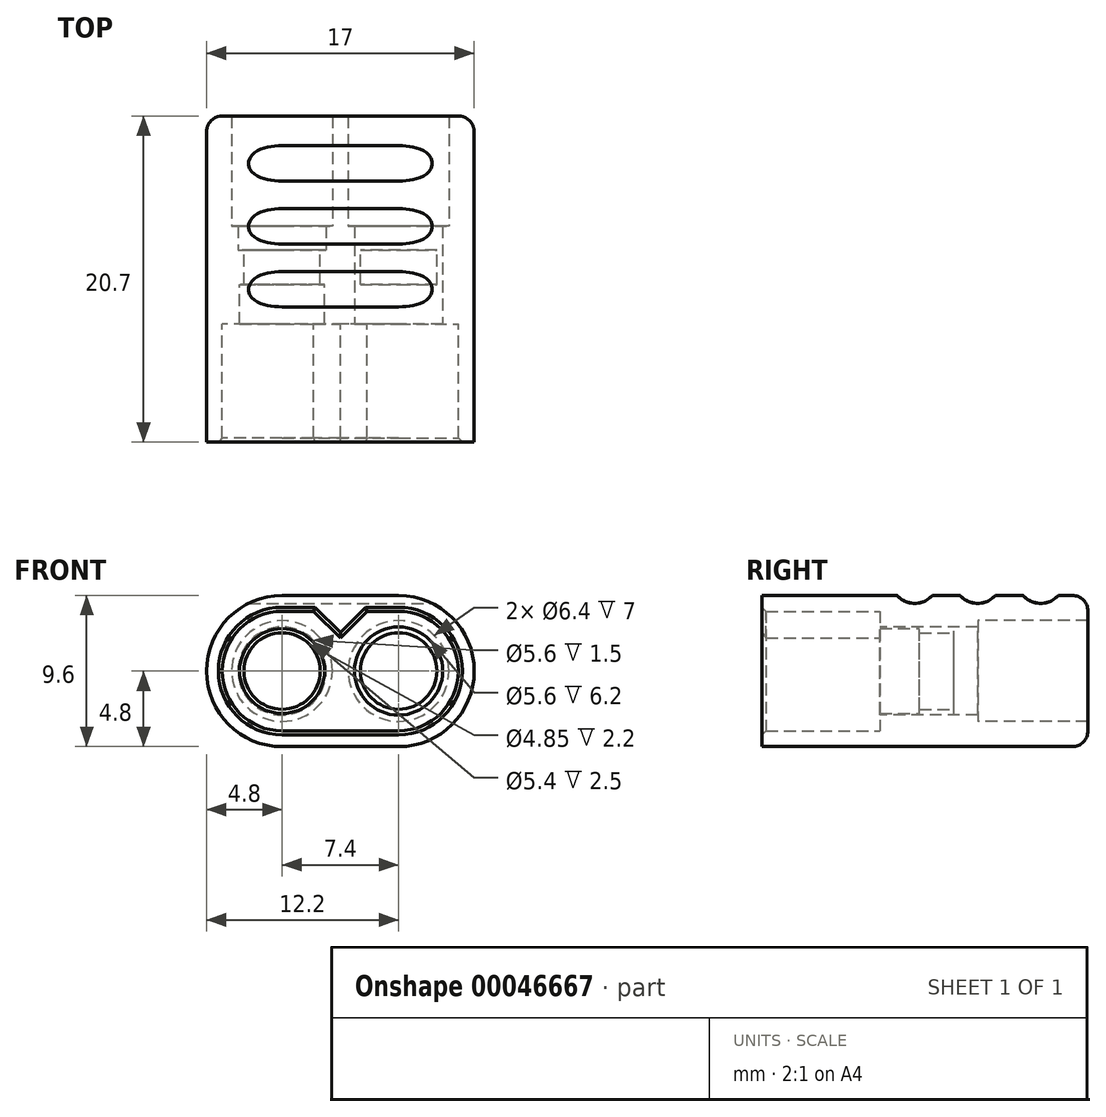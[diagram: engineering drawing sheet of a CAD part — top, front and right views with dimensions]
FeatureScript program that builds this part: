
annotation { "Feature Type Name" : "Feature", "Feature Type Description" : "" }
export const myFeature = defineFeature(function(context is Context, id is Id, definition is map)
    precondition{}
    {
        {
            var Q0;
            Q0=qCreatedBy(makeId("Front.planeOp"),FACE);
            var sketch = newSketch(context, id + "F0", { "sketchPlane" : qUnion([Q0])});
            skCircle(sketch, "E0", {"center": v(-3.7, 0) * mm, "radius": 2.43 * mm});
            skCircle(sketch, "E1.MirrorC", {"center": v(-3.7, 0) * mm, "radius": 2.8 * mm});
            skLineSegment(sketch, "E2", {"start": v(0, 0) * mm, "end": v(-8.5, 0) * mm, "construction": true});
            skArc(sketch, "E3", {"start": v(-3.7, 4.8) * mm, "mid": v(-7.1, 3.4) * mm, "end": v(-8.5, 0) * mm});
            skLineSegment(sketch, "E4", {"start": v(0, 4.8) * mm, "end": v(0, 0) * mm, "construction": true});
            skLineSegment(sketch, "E5", {"start": v(-3.7, 4.8) * mm, "end": v(-3.7, 0) * mm, "construction": true});
            skCircle(sketch, "E6.MirrorC", {"center": v(3.7, 0) * mm, "radius": 2.43 * mm});
            skCircle(sketch, "E7.MirrorC", {"center": v(3.7, 0) * mm, "radius": 2.8 * mm});
            skLineSegment(sketch, "E8", {"start": v(-3.7, 4.8) * mm, "end": v(0, 4.8) * mm});
            skArc(sketch, "E9.MirrorCS", {"start": v(-3.7, -4.8) * mm, "mid": v(-7.1, -3.4) * mm, "end": v(-8.5, 0) * mm});
            skLineSegment(sketch, "E10.MirrorCS", {"start": v(-3.7, -4.8) * mm, "end": v(0, -4.8) * mm});
            skLineSegment(sketch, "E11.MirrorCS", {"start": v(3.7, 4.8) * mm, "end": v(0, 4.8) * mm});
            skArc(sketch, "E12.MirrorCS", {"start": v(3.7, 4.8) * mm, "mid": v(7.1, 3.4) * mm, "end": v(8.5, 0) * mm});
            skArc(sketch, "E13.MirrorCS", {"start": v(3.7, -4.8) * mm, "mid": v(7.1, -3.4) * mm, "end": v(8.5, 0) * mm});
            skLineSegment(sketch, "E14.MirrorCS", {"start": v(3.7, -4.8) * mm, "end": v(0, -4.8) * mm});
            skSolve(sketch);
        }
        {
            var Q0;
            Q0=makeQuery(id+"F0.imprint","IMPRINT",FACE,{"disambiguationData":[TD([[makeQuery(id+"F0.imprint","IMPRINT",EDGE,{"derivedFrom":sQuery(id+"F0.wireOp",EDGE,"E1.MirrorC")}),-1.0]])]});
            extrude(context, id + "F1", {"entities" : qUnion([Q0]), "oppositeDirection" : true, "depth" : 1.5 * mm});
        }
        {
            var Q0;
            Q0=makeQuery(id+"F0.imprint","IMPRINT",FACE,{"disambiguationData":[TD([[makeQuery(id+"F0.imprint","IMPRINT",EDGE,{"derivedFrom":sQuery(id+"F0.wireOp",EDGE,"E1.MirrorC")}),-1.0]])]});
            var Q1;
            Q1=makeQuery(id+"F0.imprint","IMPRINT",FACE,{"disambiguationData":[TD([[makeQuery(id+"F0.imprint","IMPRINT",EDGE,{"derivedFrom":sQuery(id+"F0.wireOp",EDGE,"E0")}),-1.0]])]});
            var Q2;
            Q2=makeQuery(id+"F0.imprint","IMPRINT",FACE,{"disambiguationData":[TD([[makeQuery(id+"F0.imprint","IMPRINT",EDGE,{"derivedFrom":sQuery(id+"F0.wireOp",EDGE,"E6.MirrorC")}),1.0]])]});
            extrude(context, id + "F2", {"entities" : qUnion([Q0, Q1, Q2]), "operationType" : NewBodyOperationType.ADD, "depth" : 2.2 * mm});
        }
        {
            var Q0;
            Q0=makeQuery(id+"F2.opExtrude","CAP_FACE",FACE,{"disambiguationData":[OSD([sQuery(id+"F0.wireOp",EDGE,"9af29b95-2ce9-48ef-83fd-eb93086e848a.bottom"),sQuery(id+"F0.wireOp",EDGE,"9af29b95-2ce9-48ef-83fd-eb93086e848a.top"),sQuery(id+"F0.wireOp",EDGE,"9af29b95-2ce9-48ef-83fd-eb93086e848a.left"),sQuery(id+"F0.wireOp",EDGE,"9af29b95-2ce9-48ef-83fd-eb93086e848a.right"),sQuery(id+"F0.wireOp",EDGE,"E0"),sQuery(id+"F0.wireOp",EDGE,"3bfeefd6-8ccf-4d28-93f8-2f2611132b7e0.MirrorC")])],"isStart":false});
            var sketch = newSketch(context, id + "F3", { "sketchPlane" : qUnion([Q0])});
            skCircle(sketch, "E15", {"center": v(-3.7, 0) * mm, "radius": 2.7 * mm});
            skCircle(sketch, "E16.MirrorC", {"center": v(3.7, 0) * mm, "radius": 2.7 * mm});
            skSolve(sketch);
        }
        {
            var Q0;
            Q0=makeQuery(id+"F3.imprint","IMPRINT",FACE,{"disambiguationData":[TD([[makeQuery(id+"F3.imprint","IMPRINT",EDGE,{"derivedFrom":sQuery(id+"F3.wireOp",EDGE,"E15")}),-1.0]])]});
            extrude(context, id + "F4", {"entities" : qUnion([Q0]), "operationType" : NewBodyOperationType.ADD, "depth" : 2.5 * mm});
        }
        {
            var Q0;
            Q0=makeQuery(id+"F4.opExtrude","CAP_FACE",FACE,{"disambiguationData":[OSD([sQuery(id+"F0.wireOp",EDGE,"6d7ef5f6-68e2-491c-bdb9-d34946de3217"),sQuery(id+"F0.wireOp",EDGE,"4a62e17a-e464-4ae6-85fd-e67879230d62"),sQuery(id+"F0.wireOp",EDGE,"d8da9cf0-fa24-4876-8edd-ab64fd6ac28d"),sQuery(id+"F0.wireOp",EDGE,"6ed2982d-5885-44c9-aeb3-c63c06cbabe1.filletArc"),sQuery(id+"F0.wireOp",EDGE,"ac0d3ca8-c71e-4b4c-905e-2867e2134c0f.filletArc"),sQuery(id+"F0.wireOp",EDGE,"db059e13-4987-40d7-b22c-4aa99c86301e0.MirrorCS"),sQuery(id+"F0.wireOp",EDGE,"21968229-6fcb-4818-9fba-464d6f3a7a490.MirrorCS"),sQuery(id+"F0.wireOp",EDGE,"27c3a9c7-bba5-4ce6-a0b2-ee3fde2fc81d0.MirrorCS"),sQuery(id+"F0.wireOp",EDGE,"74e78b0a-03c2-4682-ad69-f2b08288fff30.MirrorCS"),sQuery(id+"F0.wireOp",EDGE,"d6014dcf-48b1-47f5-9b02-8fcda7855cd30.MirrorCS"),sQuery(id+"F3.wireOp",EDGE,"E15"),sQuery(id+"F3.wireOp",EDGE,"3893830b-eff6-4bac-9637-d990255e7b810.MirrorC")])],"isStart":false});
            var sketch = newSketch(context, id + "F5", { "sketchPlane" : qUnion([Q0])});
            skLineSegment(sketch, "E17", {"start": v(-3.7, -3.8) * mm, "end": v(0, -3.8) * mm});
            skLineSegment(sketch, "E18", {"start": v(-1.7, 3.8) * mm, "end": v(0, 2.1) * mm});
            skArc(sketch, "E19", {"start": v(-3.7, 3.8) * mm, "mid": v(-7.5, 0) * mm, "end": v(-3.7, -3.8) * mm});
            skLineSegment(sketch, "E20", {"start": v(-3.7, 3.8) * mm, "end": v(-1.7, 3.8) * mm});
            skLineSegment(sketch, "E21.MirrorCS", {"start": v(1.7, 3.8) * mm, "end": v(0, 2.1) * mm});
            skLineSegment(sketch, "E22.MirrorCS", {"start": v(3.7, 3.8) * mm, "end": v(1.7, 3.8) * mm});
            skArc(sketch, "E23.MirrorCS", {"start": v(3.7, 3.8) * mm, "mid": v(7.5, 0) * mm, "end": v(3.7, -3.8) * mm});
            skLineSegment(sketch, "E24.MirrorCS", {"start": v(3.7, -3.8) * mm, "end": v(0, -3.8) * mm});
            skSolve(sketch);
        }
        {
            var Q0;
            Q0=makeQuery(id+"F5.imprint","IMPRINT",FACE,{"disambiguationData":[TD([[makeQuery(id+"F5.imprint","IMPRINT",EDGE,{"derivedFrom":sQuery(id+"F5.wireOp",EDGE,"E17")}),-1.0]])]});
            extrude(context, id + "F6", {"entities" : qUnion([Q0]), "operationType" : NewBodyOperationType.ADD, "depth" : 7.5 * mm});
        }
        {
            var Q0;
            Q0=makeQuery(id+"F1.opExtrude","CAP_FACE",FACE,{"disambiguationData":[OSD([sQuery(id+"F0.wireOp",EDGE,"E1.MirrorC"),sQuery(id+"F0.wireOp",EDGE,"E3"),sQuery(id+"F0.wireOp",EDGE,"E7.MirrorC"),sQuery(id+"F0.wireOp",EDGE,"E8"),sQuery(id+"F0.wireOp",EDGE,"E9.MirrorCS"),sQuery(id+"F0.wireOp",EDGE,"E10.MirrorCS"),sQuery(id+"F0.wireOp",EDGE,"E11.MirrorCS"),sQuery(id+"F0.wireOp",EDGE,"E12.MirrorCS"),sQuery(id+"F0.wireOp",EDGE,"E13.MirrorCS"),sQuery(id+"F0.wireOp",EDGE,"E14.MirrorCS")])],"isStart":false});
            var sketch = newSketch(context, id + "F7", { "sketchPlane" : qUnion([Q0])});
            skCircle(sketch, "E25", {"center": v(3.7, 0) * mm, "radius": 3.2 * mm});
            skCircle(sketch, "E26.MirrorC", {"center": v(-3.7, 0) * mm, "radius": 3.2 * mm});
            skSolve(sketch);
        }
        {
            var Q0;
            Q0=makeQuery(id+"F7.imprint","IMPRINT",FACE,{"disambiguationData":[TD([[makeQuery(id+"F7.imprint","IMPRINT",EDGE,{"derivedFrom":sQuery(id+"F7.wireOp",EDGE,"E25")}),-1.0]])]});
            extrude(context, id + "F8", {"entities" : qUnion([Q0]), "operationType" : NewBodyOperationType.ADD, "depth" : 7 * mm});
        }
        {
            var Q0;
            Q0=makeQuery(id+"F8.opExtrude","CAP_EDGE",EDGE,{"disambiguationData":[OSD([sQuery(id+"F0.wireOp",EDGE,"E8"),sQuery(id+"F0.wireOp",EDGE,"E11.MirrorCS")])],"isStart":false});
            fillet(context, id + "F9", {"entities" : qUnion([Q0]), "radius" : 1 * mm, "tangentPropagation" : true, "allowEdgeOverflow" : false});
        }
        {
            var Q0;
            Q0=makeQuery(id+"F6.opExtrude","CAP_EDGE",EDGE,{"disambiguationData":[OSD([sQuery(id+"F5.wireOp",EDGE,"E19")])],"isStart":false});
            var Q1;
            Q1=makeQuery(id+"F6.opExtrude","CAP_EDGE",EDGE,{"disambiguationData":[OSD([sQuery(id+"F5.wireOp",EDGE,"E20")])],"isStart":false});
            var Q2;
            Q2=makeQuery(id+"F6.opExtrude","CAP_EDGE",EDGE,{"disambiguationData":[OSD([sQuery(id+"F5.wireOp",EDGE,"E18")])],"isStart":false});
            var Q3;
            Q3=makeQuery(id+"F6.opExtrude","CAP_EDGE",EDGE,{"disambiguationData":[OSD([sQuery(id+"F5.wireOp",EDGE,"E21.MirrorCS")])],"isStart":false});
            var Q4;
            Q4=makeQuery(id+"F6.opExtrude","CAP_EDGE",EDGE,{"disambiguationData":[OSD([sQuery(id+"F5.wireOp",EDGE,"E22.MirrorCS")])],"isStart":false});
            var Q5;
            Q5=makeQuery(id+"F6.opExtrude","CAP_EDGE",EDGE,{"disambiguationData":[OSD([sQuery(id+"F5.wireOp",EDGE,"E23.MirrorCS")])],"isStart":false});
            var Q6;
            Q6=makeQuery(id+"F6.opExtrude","CAP_EDGE",EDGE,{"disambiguationData":[OSD([sQuery(id+"F5.wireOp",EDGE,"E17"),sQuery(id+"F5.wireOp",EDGE,"E24.MirrorCS")])],"isStart":false});
            chamfer(context, id + "F10", {"entities" : qUnion([Q0, Q1, Q2, Q3, Q4, Q5, Q6]), "width" : 0.25 * mm, "tangentPropagation" : true});
        }
        {
            var Q0;
            Q0=qCreatedBy(makeId("Right.planeOp"),FACE);
            var sketch = newSketch(context, id + "F11", { "sketchPlane" : qUnion([Q0])});
            skCircle(sketch, "E27", {"center": v(-2.5, 5.8) * mm, "radius": 1.5 * mm});
            skCircle(sketch, "E28", {"center": v(5.5, 5.8) * mm, "radius": 1.5 * mm});
            skLineSegment(sketch, "E29", {"start": v(9.5, 0) * mm, "end": v(-15.5, 0) * mm, "construction": true});
            skLineSegment(sketch, "E30", {"start": v(-2.5, 5.8) * mm, "end": v(5.5, 5.8) * mm, "construction": true});
            skCircle(sketch, "E31", {"center": v(1.5, 5.8) * mm, "radius": 1.5 * mm});
            skCircle(sketch, "E32.MirrorC", {"center": v(1.5, -5.8) * mm, "radius": 1.5 * mm});
            skCircle(sketch, "E33.MirrorC", {"center": v(-2.5, -5.8) * mm, "radius": 1.5 * mm});
            skCircle(sketch, "E34.MirrorC", {"center": v(5.5, -5.8) * mm, "radius": 1.5 * mm});
            skSolve(sketch);
        }
        {
            var Q0;
            Q0=makeQuery(id+"F11.imprint","IMPRINT",FACE,{"disambiguationData":[TD([[makeQuery(id+"F11.imprint","IMPRINT",EDGE,{"derivedFrom":sQuery(id+"F11.wireOp",EDGE,"E27")}),1.0]])]});
            var Q1;
            Q1=makeQuery(id+"F11.imprint","IMPRINT",FACE,{"disambiguationData":[TD([[makeQuery(id+"F11.imprint","IMPRINT",EDGE,{"derivedFrom":sQuery(id+"F11.wireOp",EDGE,"E31")}),1.0]])]});
            var Q2;
            Q2=makeQuery(id+"F11.imprint","IMPRINT",FACE,{"disambiguationData":[TD([[makeQuery(id+"F11.imprint","IMPRINT",EDGE,{"derivedFrom":sQuery(id+"F11.wireOp",EDGE,"E28")}),1.0]])]});
            var Q3;
            Q3=makeQuery(id+"F11.imprint","IMPRINT",FACE,{"disambiguationData":[TD([[makeQuery(id+"F11.imprint","IMPRINT",EDGE,{"derivedFrom":sQuery(id+"F11.wireOp",EDGE,"E33.MirrorC")}),-1.0]])]});
            var Q4;
            Q4=makeQuery(id+"F11.imprint","IMPRINT",FACE,{"disambiguationData":[TD([[makeQuery(id+"F11.imprint","IMPRINT",EDGE,{"derivedFrom":sQuery(id+"F11.wireOp",EDGE,"E32.MirrorC")}),-1.0]])]});
            var Q5;
            Q5=makeQuery(id+"F11.imprint","IMPRINT",FACE,{"disambiguationData":[TD([[makeQuery(id+"F11.imprint","IMPRINT",EDGE,{"derivedFrom":sQuery(id+"F11.wireOp",EDGE,"E34.MirrorC")}),-1.0]])]});
            extrude(context, id + "F12", {"entities" : qUnion([Q0, Q1, Q2, Q3, Q4, Q5]), "operationType" : NewBodyOperationType.REMOVE, "endBound" : BoundingType.SYMMETRIC, "oppositeDirection" : true, "depth" : 17 * mm});
        }
    });
